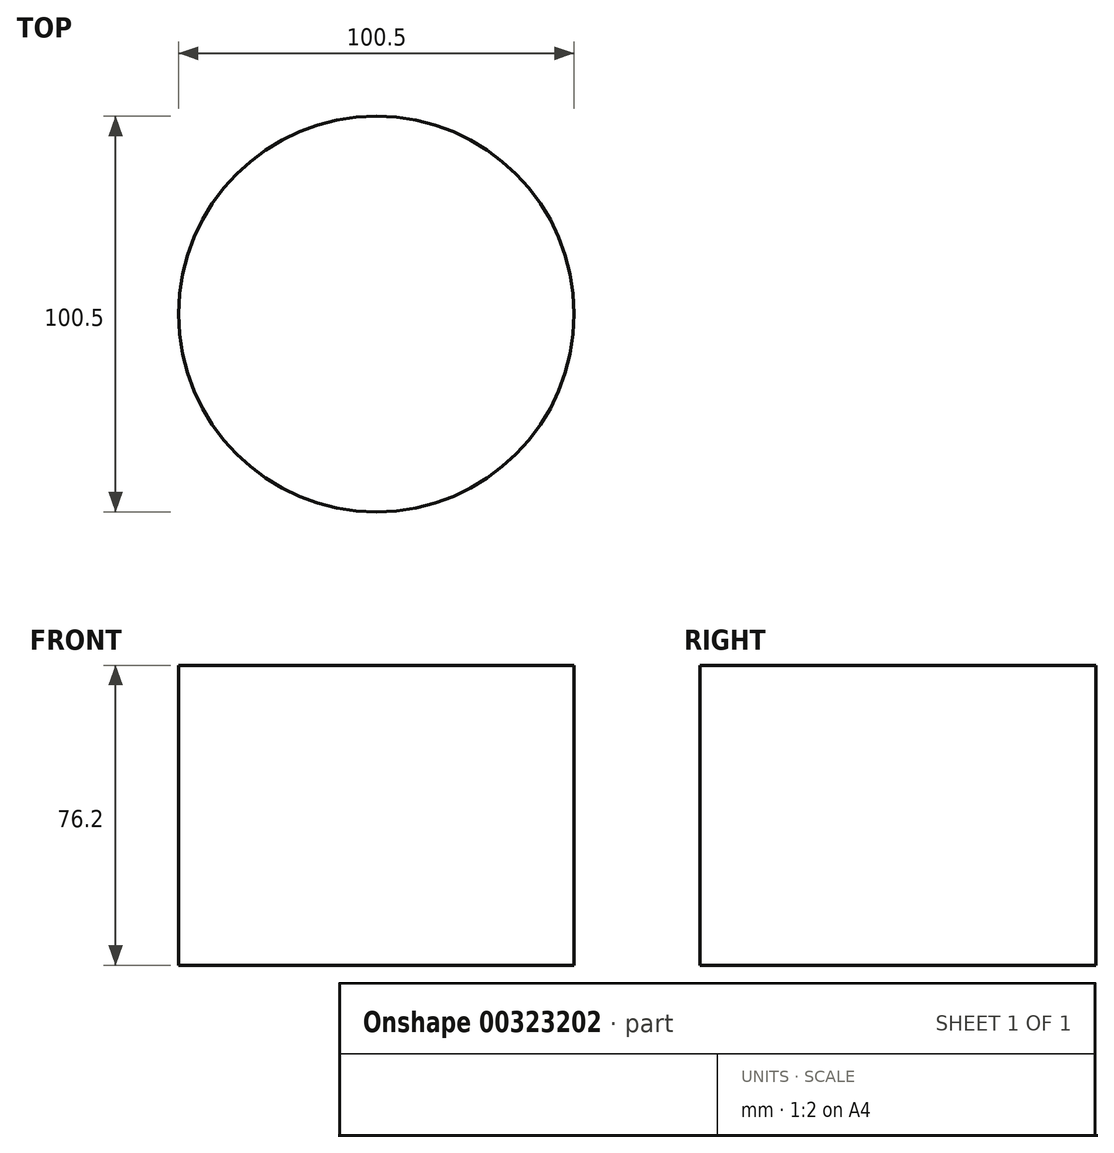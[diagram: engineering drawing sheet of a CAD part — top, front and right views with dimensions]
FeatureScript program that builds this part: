
annotation { "Feature Type Name" : "Feature", "Feature Type Description" : "" }
export const myFeature = defineFeature(function(context is Context, id is Id, definition is map)
    precondition{}
    {
        {
            var Q0;
            Q0=qCreatedBy(makeId("Top.planeOp"),FACE);
            var sketch = newSketch(context, id + "F0", { "sketchPlane" : qUnion([Q0])});
            skCircle(sketch, "E0", {"center": v(0, 0) * mm, "radius": 50.25 * mm});
            skSolve(sketch);
        }
        {
            var Q0;
            Q0 = qSketchRegion(id + "F0", true);
            extrude(context, id + "F1", {"entities" : qUnion([Q0]), "depth" : 76.2 * mm});
        }
    });
